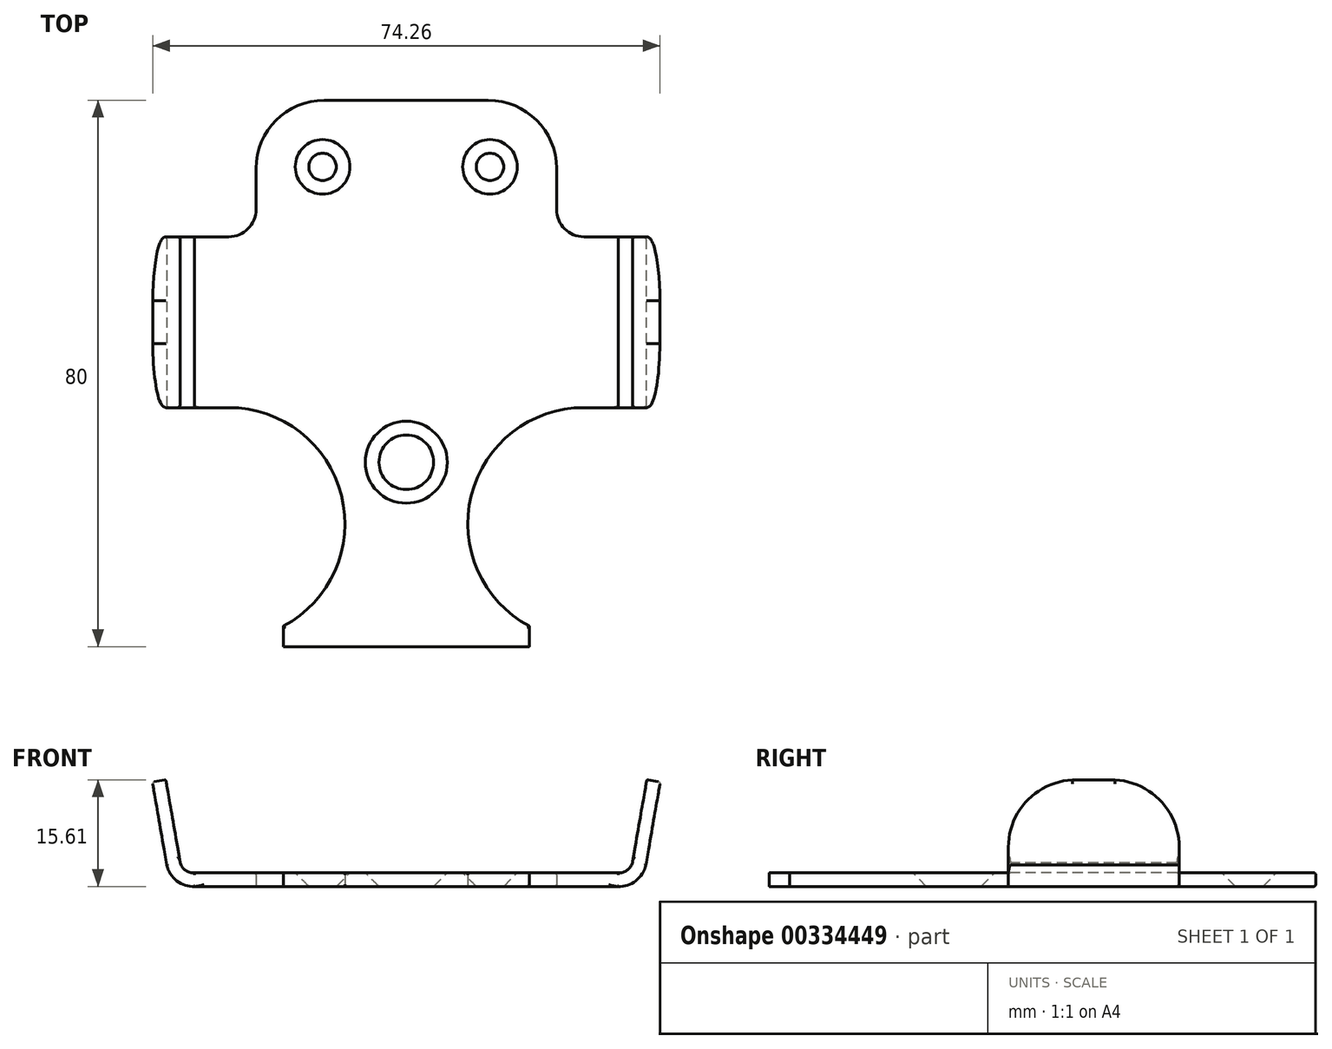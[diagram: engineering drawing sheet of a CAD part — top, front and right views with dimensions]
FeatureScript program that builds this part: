
annotation { "Feature Type Name" : "Feature", "Feature Type Description" : "" }
export const myFeature = defineFeature(function(context is Context, id is Id, definition is map)
    precondition{}
    {
        {
            var Q0;
            Q0=qCreatedBy(makeId("Top.planeOp"),FACE);
            var sketch = newSketch(context, id + "F0", { "sketchPlane" : qUnion([Q0])});
            skLineSegment(sketch, "E0", {"start": v(0, 38) * mm, "end": v(0, -42) * mm, "construction": true});
            skLineSegment(sketch, "E1", {"start": v(0, 38) * mm, "end": v(-12, 38) * mm});
            skArc(sketch, "E2", {"start": v(-12, 38) * mm, "mid": v(-19.07, 35.07) * mm, "end": v(-22, 28) * mm});
            skLineSegment(sketch, "E3", {"start": v(-22, 28) * mm, "end": v(-22, 22) * mm});
            skArc(sketch, "E4", {"start": v(-26, 18) * mm, "mid": v(-23.17, 19.17) * mm, "end": v(-22, 22) * mm});
            skLineSegment(sketch, "E5", {"start": v(-26, 18) * mm, "end": v(-28.5, 18) * mm});
            skLineSegment(sketch, "E6", {"start": v(-28.5, 18) * mm, "end": v(-28.5, -7) * mm});
            skLineSegment(sketch, "E7", {"start": v(-28.5, -7) * mm, "end": v(-26, -7) * mm});
            skArc(sketch, "E8", {"start": v(-18, -39) * mm, "mid": v(-9.5, -19.88) * mm, "end": v(-26, -7) * mm});
            skLineSegment(sketch, "E9", {"start": v(-18, -39) * mm, "end": v(-18, -42) * mm});
            skLineSegment(sketch, "E10", {"start": v(-18, -42) * mm, "end": v(0, -42) * mm});
            skLineSegment(sketch, "E11.MirrorCS", {"start": v(0, 38) * mm, "end": v(12, 38) * mm});
            skArc(sketch, "E12.MirrorCS", {"start": v(12, 38) * mm, "mid": v(19.07, 35.07) * mm, "end": v(22, 28) * mm});
            skLineSegment(sketch, "E13.MirrorCS", {"start": v(22, 28) * mm, "end": v(22, 22) * mm});
            skArc(sketch, "E14.MirrorCS", {"start": v(26, 18) * mm, "mid": v(23.17, 19.17) * mm, "end": v(22, 22) * mm});
            skLineSegment(sketch, "E15.MirrorCS", {"start": v(26, 18) * mm, "end": v(28.5, 18) * mm});
            skLineSegment(sketch, "E16.MirrorCS", {"start": v(28.5, 18) * mm, "end": v(28.5, -7) * mm});
            skLineSegment(sketch, "E17.MirrorCS", {"start": v(28.5, -7) * mm, "end": v(26, -7) * mm});
            skArc(sketch, "E18.MirrorCS", {"start": v(18, -39) * mm, "mid": v(9.5, -19.88) * mm, "end": v(26, -7) * mm});
            skLineSegment(sketch, "E19.MirrorCS", {"start": v(18, -39) * mm, "end": v(18, -42) * mm});
            skLineSegment(sketch, "E20.MirrorCS", {"start": v(18, -42) * mm, "end": v(0, -42) * mm});
            skSolve(sketch);
        }
        {
            var Q0;
            Q0 = qSketchRegion(id + "F0", true);
            var Q1;
            Q1=makeQuery(id+"F0.imprint","IMPRINT",FACE,{"disambiguationData":[TD([[makeQuery(id+"F0.imprint","IMPRINT",EDGE,{"derivedFrom":sQuery(id+"F0.wireOp",EDGE,"E1")}),1.0]])]});
            extrude(context, id + "F1", {"entities" : qUnion([Q0, Q1]), "depth" : 2 * mm});
        }
        {
            var Q0;
            Q0=makeQuery(id+"F1.opExtrude","SWEPT_FACE",FACE,{"disambiguationData":[OSD([sQuery(id+"F0.wireOp",EDGE,"E7")])]});
            var sketch = newSketch(context, id + "F2", { "sketchPlane" : qUnion([Q0])});
            skLineSegment(sketch, "E21", {"start": v(-28.5, 0) * mm, "end": v(-31, 0) * mm});
            skArc(sketch, "E22", {"start": v(-35.07, 3.15) * mm, "mid": v(-33.6, 0.83) * mm, "end": v(-31, 0) * mm});
            skLineSegment(sketch, "E23", {"start": v(-35.07, 3.15) * mm, "end": v(-35.47, 5.47) * mm});
            skLineSegment(sketch, "E24", {"start": v(-35.47, 5.47) * mm, "end": v(-33.5, 5.8) * mm});
            skLineSegment(sketch, "E25", {"start": v(-33.5, 5.8) * mm, "end": v(-33.1, 3.5) * mm});
            skArc(sketch, "E26", {"start": v(-33.1, 3.5) * mm, "mid": v(-32.32, 2.36) * mm, "end": v(-31, 2) * mm});
            skLineSegment(sketch, "E27", {"start": v(-28.5, 2) * mm, "end": v(-31, 2) * mm});
            skSolve(sketch);
        }
        {
            var Q0;
            Q0=makeQuery(id+"F2.imprint","IMPRINT",FACE,{"disambiguationData":[TD([[makeQuery(id+"F2.imprint","IMPRINT",EDGE,{"derivedFrom":sQuery(id+"F2.wireOp",EDGE,"E21")}),-1.0]])]});
            extrude(context, id + "F3", {"entities" : qUnion([Q0]), "oppositeDirection" : true, "depth" : 25 * mm});
        }
        {
            var Q0;
            Q0=makeQuery(id+"F3.opExtrude","SWEPT_FACE",FACE,{"disambiguationData":[OSD([sQuery(id+"F2.wireOp",EDGE,"E23")])]});
            var sketch = newSketch(context, id + "F4", { "sketchPlane" : qUnion([Q0])});
            skArc(sketch, "E28", {"start": v(-8.64, 21.44) * mm, "mid": v(-15.3, 18.3) * mm, "end": v(-18, 11.46) * mm});
            skArc(sketch, "E29", {"start": v(7, 11.46) * mm, "mid": v(4.3, 18.3) * mm, "end": v(-2.36, 21.44) * mm});
            skLineSegment(sketch, "E30", {"start": v(-8.64, 21.44) * mm, "end": v(-2.36, 21.44) * mm});
            skSolve(sketch);
        }
        {
            var Q0;
            Q0=makeQuery(id+"F4.imprint","IMPRINT",FACE,{"disambiguationData":[TD([[makeQuery(id+"F4.imprint","IMPRINT",EDGE,{"derivedFrom":sQuery(id+"F4.wireOp",EDGE,"E28")}),1.0]])]});
            extrude(context, id + "F5", {"entities" : qUnion([Q0]), "operationType" : NewBodyOperationType.ADD, "oppositeDirection" : true, "depth" : 2 * mm});
        }
        {
            var Q0;
            Q0=makeQuery(id+"F3.opExtrude","SWEPT_BODY",BODY,{"disambiguationData":[OSD([sQuery(id+"F0.wireOp",EDGE,"E6"),sQuery(id+"F0.wireOp",EDGE,"E7"),sQuery(id+"F2.wireOp",EDGE,"E21"),sQuery(id+"F2.wireOp",EDGE,"E22"),sQuery(id+"F2.wireOp",EDGE,"E23"),sQuery(id+"F2.wireOp",EDGE,"E24"),sQuery(id+"F2.wireOp",EDGE,"E25"),sQuery(id+"F2.wireOp",EDGE,"E26"),sQuery(id+"F2.wireOp",EDGE,"E27")])]});
            var Q1;
            Q1=qCreatedBy(makeId("Right.planeOp"),FACE);
            mirror(context, id + "F6", {"operationType" : NewBodyOperationType.ADD, "entities" : qUnion([Q0]), "mirrorPlane" : qUnion([Q1])});
        }
        {
            var Q0;
            {var subQ0=makeQuery(id+"F3.opExtrude","SWEPT_FACE",FACE,{"disambiguationData":[OSD([sQuery(id+"F2.wireOp",EDGE,"E27")])]});Q0=makeQuery(id+"F6.boolean.opBoolean","MERGE",FACE,{"derivedFrom":[makeQuery(id+"F1.opExtrude","CAP_FACE",FACE,{"disambiguationData":[OSD([sQuery(id+"F0.wireOp",EDGE,"E1"),sQuery(id+"F0.wireOp",EDGE,"E2"),sQuery(id+"F0.wireOp",EDGE,"E3"),sQuery(id+"F0.wireOp",EDGE,"E4"),sQuery(id+"F0.wireOp",EDGE,"E5"),sQuery(id+"F0.wireOp",EDGE,"E6"),sQuery(id+"F0.wireOp",EDGE,"E7"),sQuery(id+"F0.wireOp",EDGE,"E8"),sQuery(id+"F0.wireOp",EDGE,"E9"),sQuery(id+"F0.wireOp",EDGE,"E11.MirrorCS"),sQuery(id+"F0.wireOp",EDGE,"E12.MirrorCS"),sQuery(id+"F0.wireOp",EDGE,"E13.MirrorCS"),sQuery(id+"F0.wireOp",EDGE,"E14.MirrorCS"),sQuery(id+"F0.wireOp",EDGE,"E15.MirrorCS"),sQuery(id+"F0.wireOp",EDGE,"E16.MirrorCS"),sQuery(id+"F0.wireOp",EDGE,"E17.MirrorCS"),sQuery(id+"F0.wireOp",EDGE,"E18.MirrorCS"),sQuery(id+"F0.wireOp",EDGE,"E19.MirrorCS"),sQuery(id+"F0.wireOp",EDGE,"E20.MirrorCS"),sQuery(id+"F0.wireOp",EDGE,"E10")])],"isStart":false}),subQ0,makeQuery(id+"F6.opPattern","COPY",FACE,{"derivedFrom":subQ0,"instanceName":"1"})]});}
            var sketch = newSketch(context, id + "F7", { "sketchPlane" : qUnion([Q0])});
            skCircle(sketch, "E31", {"center": v(-12.25, 28.25) * mm, "radius": 2 * mm});
            skCircle(sketch, "E32", {"center": v(12.25, 28.25) * mm, "radius": 2 * mm});
            skCircle(sketch, "E33", {"center": v(0, -15) * mm, "radius": 4 * mm});
            skSolve(sketch);
        }
        {
            var Q0;
            Q0=sQuery(id+"F7.wireOp",VERTEX,"E31.center");
            var Q1;
            Q1=sQuery(id+"F7.wireOp",VERTEX,"E32.center");
            var Q2;
            Q2=makeQuery(id+"F1.opExtrude","SWEPT_BODY",BODY,{"disambiguationData":[OSD([sQuery(id+"F0.wireOp",EDGE,"E1"),sQuery(id+"F0.wireOp",EDGE,"E2"),sQuery(id+"F0.wireOp",EDGE,"E3"),sQuery(id+"F0.wireOp",EDGE,"E4"),sQuery(id+"F0.wireOp",EDGE,"E5"),sQuery(id+"F0.wireOp",EDGE,"E6"),sQuery(id+"F0.wireOp",EDGE,"E7"),sQuery(id+"F0.wireOp",EDGE,"E8"),sQuery(id+"F0.wireOp",EDGE,"E9"),sQuery(id+"F0.wireOp",EDGE,"E11.MirrorCS"),sQuery(id+"F0.wireOp",EDGE,"E12.MirrorCS"),sQuery(id+"F0.wireOp",EDGE,"E13.MirrorCS"),sQuery(id+"F0.wireOp",EDGE,"E14.MirrorCS"),sQuery(id+"F0.wireOp",EDGE,"E15.MirrorCS"),sQuery(id+"F0.wireOp",EDGE,"E16.MirrorCS"),sQuery(id+"F0.wireOp",EDGE,"E17.MirrorCS"),sQuery(id+"F0.wireOp",EDGE,"E18.MirrorCS"),sQuery(id+"F0.wireOp",EDGE,"E19.MirrorCS"),sQuery(id+"F0.wireOp",EDGE,"E20.MirrorCS"),sQuery(id+"F0.wireOp",EDGE,"E10")])]});
            hole(context, id + "F8", {"style" : HoleStyle.C_SINK, "endStyle" : HoleEndStyle.THROUGH, "holeDiameter" : 4 * mm, "cSinkDiameter" : 8 * mm, "cSinkAngle" : 90 * degree, "isTappedThrough" : true, "tappedDepth" : 12 * mm, "tapClearance" : 3, "locations" : qUnion([Q0, Q1]), "scope" : qUnion([Q2]), "startStyle" : HoleStartStyle.PART});
        }
        {
            var Q0;
            Q0=sQuery(id+"F7.wireOp",VERTEX,"E33.center");
            var Q1;
            Q1=makeQuery(id+"F1.opExtrude","SWEPT_BODY",BODY,{"disambiguationData":[OSD([sQuery(id+"F0.wireOp",EDGE,"E1"),sQuery(id+"F0.wireOp",EDGE,"E2"),sQuery(id+"F0.wireOp",EDGE,"E3"),sQuery(id+"F0.wireOp",EDGE,"E4"),sQuery(id+"F0.wireOp",EDGE,"E5"),sQuery(id+"F0.wireOp",EDGE,"E6"),sQuery(id+"F0.wireOp",EDGE,"E7"),sQuery(id+"F0.wireOp",EDGE,"E8"),sQuery(id+"F0.wireOp",EDGE,"E9"),sQuery(id+"F0.wireOp",EDGE,"E11.MirrorCS"),sQuery(id+"F0.wireOp",EDGE,"E12.MirrorCS"),sQuery(id+"F0.wireOp",EDGE,"E13.MirrorCS"),sQuery(id+"F0.wireOp",EDGE,"E14.MirrorCS"),sQuery(id+"F0.wireOp",EDGE,"E15.MirrorCS"),sQuery(id+"F0.wireOp",EDGE,"E16.MirrorCS"),sQuery(id+"F0.wireOp",EDGE,"E17.MirrorCS"),sQuery(id+"F0.wireOp",EDGE,"E18.MirrorCS"),sQuery(id+"F0.wireOp",EDGE,"E19.MirrorCS"),sQuery(id+"F0.wireOp",EDGE,"E20.MirrorCS"),sQuery(id+"F0.wireOp",EDGE,"E10")])]});
            hole(context, id + "F9", {"style" : HoleStyle.C_SINK, "endStyle" : HoleEndStyle.THROUGH, "holeDiameter" : 8 * mm, "cSinkDiameter" : 12 * mm, "cSinkAngle" : 90 * degree, "isTappedThrough" : true, "tappedDepth" : 12 * mm, "tapClearance" : 3, "locations" : qUnion([Q0]), "scope" : qUnion([Q1]), "startStyle" : HoleStartStyle.PART});
        }
        {
            var Q0;
            Q0=makeQuery(id+"F1.opExtrude","CAP_EDGE",EDGE,{"disambiguationData":[OSD([sQuery(id+"F0.wireOp",EDGE,"E19.MirrorCS")])],"isStart":true});
            var Q1;
            Q1=makeQuery(id+"F1.opExtrude","CAP_EDGE",EDGE,{"disambiguationData":[OSD([sQuery(id+"F0.wireOp",EDGE,"E18.MirrorCS")])],"isStart":true});
            var Q2;
            Q2=makeQuery(id+"F1.opExtrude","CAP_EDGE",EDGE,{"disambiguationData":[OSD([sQuery(id+"F0.wireOp",EDGE,"E18.MirrorCS")])],"isStart":false});
            var Q3;
            Q3=makeQuery(id+"F1.opExtrude","CAP_EDGE",EDGE,{"disambiguationData":[OSD([sQuery(id+"F0.wireOp",EDGE,"E19.MirrorCS")])],"isStart":false});
            var Q4;
            Q4=makeQuery(id+"F1.opExtrude","CAP_EDGE",EDGE,{"disambiguationData":[OSD([sQuery(id+"F0.wireOp",EDGE,"E8")])],"isStart":true});
            var Q5;
            Q5=makeQuery(id+"F1.opExtrude","CAP_EDGE",EDGE,{"disambiguationData":[OSD([sQuery(id+"F0.wireOp",EDGE,"E9")])],"isStart":true});
            var Q6;
            Q6=makeQuery(id+"F1.opExtrude","CAP_EDGE",EDGE,{"disambiguationData":[OSD([sQuery(id+"F0.wireOp",EDGE,"E9")])],"isStart":false});
            var Q7;
            Q7=makeQuery(id+"F1.opExtrude","CAP_EDGE",EDGE,{"disambiguationData":[OSD([sQuery(id+"F0.wireOp",EDGE,"E12.MirrorCS")])],"isStart":false});
            var Q8;
            Q8=makeQuery(id+"F1.opExtrude","CAP_EDGE",EDGE,{"disambiguationData":[OSD([sQuery(id+"F0.wireOp",EDGE,"E2")])],"isStart":false});
            var Q9;
            Q9=makeQuery(id+"F1.opExtrude","CAP_EDGE",EDGE,{"disambiguationData":[OSD([sQuery(id+"F0.wireOp",EDGE,"E8")])],"isStart":false});
            var Q10;
            Q10=makeQuery(id+"F6.opPattern","COPY",EDGE,{"derivedFrom":makeQuery(id+"F5.opExtrude","CAP_EDGE",EDGE,{"disambiguationData":[OSD([sQuery(id+"F4.wireOp",EDGE,"E30")])],"isStart":true}),"instanceName":"1"});
            var Q11;
            Q11=makeQuery(id+"F6.opPattern","COPY",EDGE,{"derivedFrom":makeQuery(id+"F5.opExtrude","CAP_EDGE",EDGE,{"disambiguationData":[OSD([sQuery(id+"F4.wireOp",EDGE,"E28")])],"isStart":true}),"instanceName":"1"});
            var Q12;
            Q12=makeQuery(id+"F6.opPattern","COPY",EDGE,{"derivedFrom":makeQuery(id+"F5.opExtrude","CAP_EDGE",EDGE,{"disambiguationData":[OSD([sQuery(id+"F4.wireOp",EDGE,"E29")])],"isStart":true}),"instanceName":"1"});
            var Q13;
            Q13=makeQuery(id+"F5.opExtrude","CAP_EDGE",EDGE,{"disambiguationData":[OSD([sQuery(id+"F4.wireOp",EDGE,"E28")])],"isStart":true});
            var Q14;
            Q14=makeQuery(id+"F5.opExtrude","CAP_EDGE",EDGE,{"disambiguationData":[OSD([sQuery(id+"F4.wireOp",EDGE,"E30")])],"isStart":true});
            var Q15;
            Q15=makeQuery(id+"F5.opExtrude","CAP_EDGE",EDGE,{"disambiguationData":[OSD([sQuery(id+"F4.wireOp",EDGE,"E29")])],"isStart":true});
            var Q16;
            Q16=makeQuery(id+"F1.opExtrude","CAP_EDGE",EDGE,{"disambiguationData":[OSD([sQuery(id+"F0.wireOp",EDGE,"E1"),sQuery(id+"F0.wireOp",EDGE,"E11.MirrorCS")])],"isStart":true});
            var Q17;
            Q17=makeQuery(id+"F1.opExtrude","CAP_EDGE",EDGE,{"disambiguationData":[OSD([sQuery(id+"F0.wireOp",EDGE,"E12.MirrorCS")])],"isStart":true});
            var Q18;
            Q18=makeQuery(id+"F1.opExtrude","CAP_EDGE",EDGE,{"disambiguationData":[OSD([sQuery(id+"F0.wireOp",EDGE,"E2")])],"isStart":true});
            var Q19;
            Q19=makeQuery(id+"F6.opPattern","COPY",EDGE,{"derivedFrom":makeQuery(id+"F3.opExtrude","CAP_EDGE",EDGE,{"disambiguationData":[OSD([sQuery(id+"F2.wireOp",EDGE,"E22")])],"isStart":false}),"instanceName":"1"});
            var Q20;
            Q20=makeQuery(id+"F3.opExtrude","CAP_EDGE",EDGE,{"disambiguationData":[OSD([sQuery(id+"F2.wireOp",EDGE,"E22")])],"isStart":false});
            fillet(context, id + "F10", {"entities" : qUnion([Q0, Q1, Q2, Q3, Q4, Q5, Q6, Q7, Q8, Q9, Q10, Q11, Q12, Q13, Q14, Q15, Q16, Q17, Q18, Q19, Q20]), "radius" : 0.3 * mm, "tangentPropagation" : true, "allowEdgeOverflow" : false});
        }
        {
            var Q0;
            Q0=makeQuery(id+"F5.opExtrude","CAP_EDGE",EDGE,{"disambiguationData":[OSD([sQuery(id+"F4.wireOp",EDGE,"E30")])],"isStart":false});
            var Q1;
            Q1=makeQuery(id+"F6.opPattern","COPY",EDGE,{"derivedFrom":makeQuery(id+"F5.opExtrude","CAP_EDGE",EDGE,{"disambiguationData":[OSD([sQuery(id+"F4.wireOp",EDGE,"E30")])],"isStart":false}),"instanceName":"1"});
            var Q2;
            Q2=makeQuery(id+"F5.opExtrude","CAP_EDGE",EDGE,{"disambiguationData":[OSD([sQuery(id+"F4.wireOp",EDGE,"E29")])],"isStart":false});
            var Q3;
            Q3=makeQuery(id+"F6.opPattern","COPY",EDGE,{"derivedFrom":makeQuery(id+"F5.opExtrude","CAP_EDGE",EDGE,{"disambiguationData":[OSD([sQuery(id+"F4.wireOp",EDGE,"E28")])],"isStart":false}),"instanceName":"1"});
            var Q4;
            Q4=makeQuery(id+"F6.opPattern","COPY",EDGE,{"derivedFrom":makeQuery(id+"F5.opExtrude","CAP_EDGE",EDGE,{"disambiguationData":[OSD([sQuery(id+"F4.wireOp",EDGE,"E29")])],"isStart":false}),"instanceName":"1"});
            var Q5;
            Q5=makeQuery(id+"F5.opExtrude","CAP_EDGE",EDGE,{"disambiguationData":[OSD([sQuery(id+"F4.wireOp",EDGE,"E28")])],"isStart":false});
            fillet(context, id + "F11", {"entities" : qUnion([Q0, Q1, Q2, Q3, Q4, Q5]), "radius" : 0.2 * mm, "tangentPropagation" : true, "allowEdgeOverflow" : false});
        }
    });
